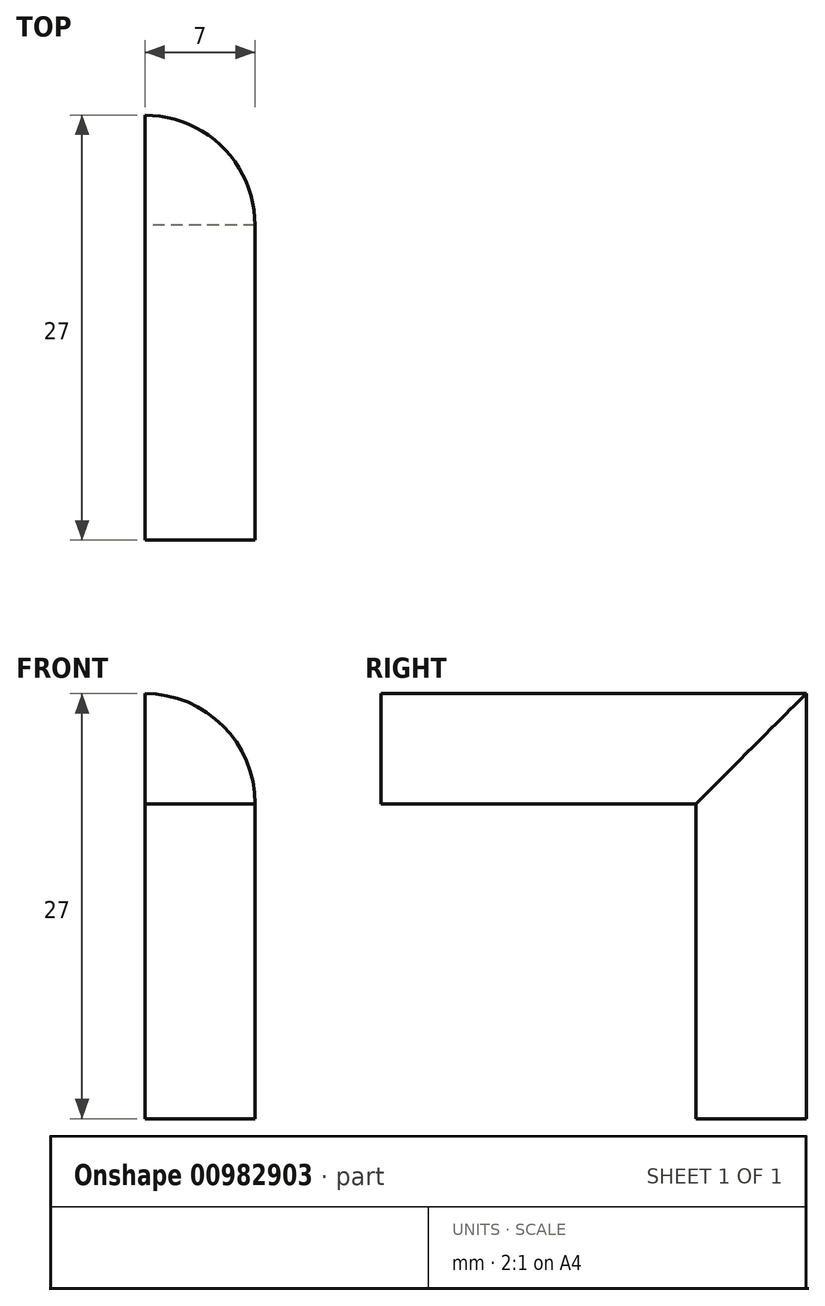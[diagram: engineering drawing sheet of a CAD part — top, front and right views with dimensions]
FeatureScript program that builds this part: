
annotation { "Feature Type Name" : "Feature", "Feature Type Description" : "" }
export const myFeature = defineFeature(function(context is Context, id is Id, definition is map)
    precondition{}
    {
        {
            var Q0;
            Q0=qCreatedBy(makeId("Top.planeOp"),FACE);
            var sketch = newSketch(context, id + "F0", { "sketchPlane" : qUnion([Q0])});
            skArc(sketch, "E0", {"start": v(7, 0) * mm, "mid": v(4.95, 4.95) * mm, "end": v(0, 7) * mm});
            skLineSegment(sketch, "E1", {"start": v(0, 0) * mm, "end": v(0, 7) * mm});
            skLineSegment(sketch, "E2", {"start": v(0, 0) * mm, "end": v(7, 0) * mm});
            skSolve(sketch);
        }
        {
            var Q0;
            Q0=makeQuery(id+"F0.imprint","IMPRINT",FACE,{"disambiguationData":[TD([[makeQuery(id+"F0.imprint","IMPRINT",EDGE,{"derivedFrom":sQuery(id+"F0.wireOp",EDGE,"E0")}),1.0]])]});
            extrude(context, id + "F1", {"entities" : qUnion([Q0]), "depth" : 15 * mm, "offsetDistance" : 25 * mm});
        }
        {
            var Q0;
            Q0=makeQuery(id+"F1.opExtrude","SWEPT_FACE",FACE,{"disambiguationData":[OSD([sQuery(id+"F0.wireOp",EDGE,"E2")])]});
            var sketch = newSketch(context, id + "F2", { "sketchPlane" : qUnion([Q0])});
            skLineSegment(sketch, "E3.0", {"start": v(0, 15) * mm, "end": v(0, 0) * mm});
            skCircle(sketch, "E4", {"center": v(0, 8) * mm, "radius": 7 * mm});
            skLineSegment(sketch, "E5", {"start": v(0, 8) * mm, "end": v(7, 8) * mm});
            skSolve(sketch);
        }
        {
            var Q0;
            {var subQ4=sQuery(id+"F2.wireOp",EDGE,"E5");Q0=makeQuery(id+"F2.imprint","IMPRINT",FACE,{"disambiguationData":[TD([[makeQuery(id+"F2.imprint","IMPRINT",EDGE,{"derivedFrom":subQ4}),1.0]])]});}
            extrude(context, id + "F3", {"entities" : qUnion([Q0]), "depth" : 15 * mm, "offsetDistance" : 25 * mm, "hasSecondDirection" : true, "secondDirectionOppositeDirection" : true, "secondDirectionDepth" : 7 * mm});
        }
        {
            var Q0;
            Q0=makeQuery(id+"F3.opExtrude","SWEPT_BODY",BODY,{"disambiguationData":[OSD([sQuery(id+"F2.wireOp",EDGE,"E3.0"),sQuery(id+"F2.wireOp",EDGE,"E4"),sQuery(id+"F2.wireOp",EDGE,"E5")])]});
            var Q1;
            Q1=makeQuery(id+"F1.opExtrude","SWEPT_BODY",BODY,{"disambiguationData":[OSD([sQuery(id+"F0.wireOp",EDGE,"E0"),sQuery(id+"F0.wireOp",EDGE,"E1"),sQuery(id+"F0.wireOp",EDGE,"E2")])]});
            booleanBodies(context, id + "F4", {"operationType" : BooleanOperationType.INTERSECTION, "tools" : qUnion([Q0, Q1])});
        }
        {
            var Q0;
            Q0=makeQuery(id+"F3.opExtrude","SWEPT_FACE",FACE,{"disambiguationData":[OSD([sQuery(id+"F2.wireOp",EDGE,"E5")])]});
            var sketch = newSketch(context, id + "F5", { "sketchPlane" : qUnion([Q0])});
            skCircle(sketch, "E6", {"center": v(0, 0) * mm, "radius": 7 * mm});
            skLineSegment(sketch, "E7", {"start": v(0, 0) * mm, "end": v(7, 0) * mm});
            skLineSegment(sketch, "E8", {"start": v(0, 0) * mm, "end": v(0, -7) * mm});
            skSolve(sketch);
        }
        {
            var Q0;
            Q0=makeQuery(id+"F1.opExtrude","SWEPT_FACE",FACE,{"disambiguationData":[OSD([sQuery(id+"F0.wireOp",EDGE,"E2")])]});
            extrude(context, id + "F6", {"entities" : qUnion([Q0]), "operationType" : NewBodyOperationType.ADD, "depth" : 20 * mm, "offsetDistance" : 25 * mm});
        }
        {
            var Q0;
            {var subQ2=sQuery(id+"F5.wireOp",EDGE,"E7");Q0=makeQuery(id+"F5.imprint","IMPRINT",FACE,{"disambiguationData":[TD([[makeQuery(id+"F5.imprint","IMPRINT",EDGE,{"derivedFrom":subQ2}),1.0]])]});}
            extrude(context, id + "F7", {"entities" : qUnion([Q0]), "operationType" : NewBodyOperationType.ADD, "depth" : 20 * mm, "offsetDistance" : 25 * mm});
        }
    });
